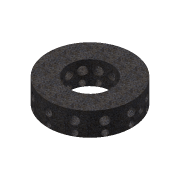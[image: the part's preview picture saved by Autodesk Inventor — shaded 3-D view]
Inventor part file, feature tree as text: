
AUTODESK INVENTOR PART (.ipt)
format: ipt  version: 2016 (Build 200138000, 138)  size: 325,120 bytes
history: native  units: in
note: dims shown in document units (in); Inventor stores cm internally (conversion verified against a paired STEP export)
features: sketch x6, extrude x3, plane x3, pattern_circular x1
ambient origin geometry x8: Origin, YZ Plane, XZ Plane, XY Plane, X Axis, Y Axis, Z Axis, Center Point
bodies: Solid1 (feature_tree)
feature tree (13):
  extrude  "Extrusion1"  Depth=10.0in TaperAngle=0.0deg
  sketch  "Sketch2"  dims[d4=18.2in d15=3.5827in d17=5.9055in]
  plane  "Work Plane1"
  sketch  "Sketch5"  dims[d18=2.5197in d19=1.3976in]
  plane  "Work Plane2"
  extrude  "Extrusion4"  Depth=3.5827in
  pattern_circular  "Circular Pattern1"  Count=15  [1 undecoded]
  sketch  "Sketch7"  dims[d22=4.7244in d23=360.0deg]
  plane  "Work Plane3"
  extrude  "Extrusion5"  Depth=1.3976in
  sketch  "Sketch1"  dims[d0=35.9in d2=10.0in d3=0.0in]
  sketch  "Sketch6"  dims[d20=10.0in d21=0.0in]
  sketch  "Sketch8"  dims[d25=20.0in d26=15.0deg d27=2.375in d28=4.0in d29=10.0in d30=0.0in]
note: 1 required parameter value undecoded (feature->parameter linkage not recoverable at this tier; creation-order binding heuristic only, values carry confidence <= 0.55)
